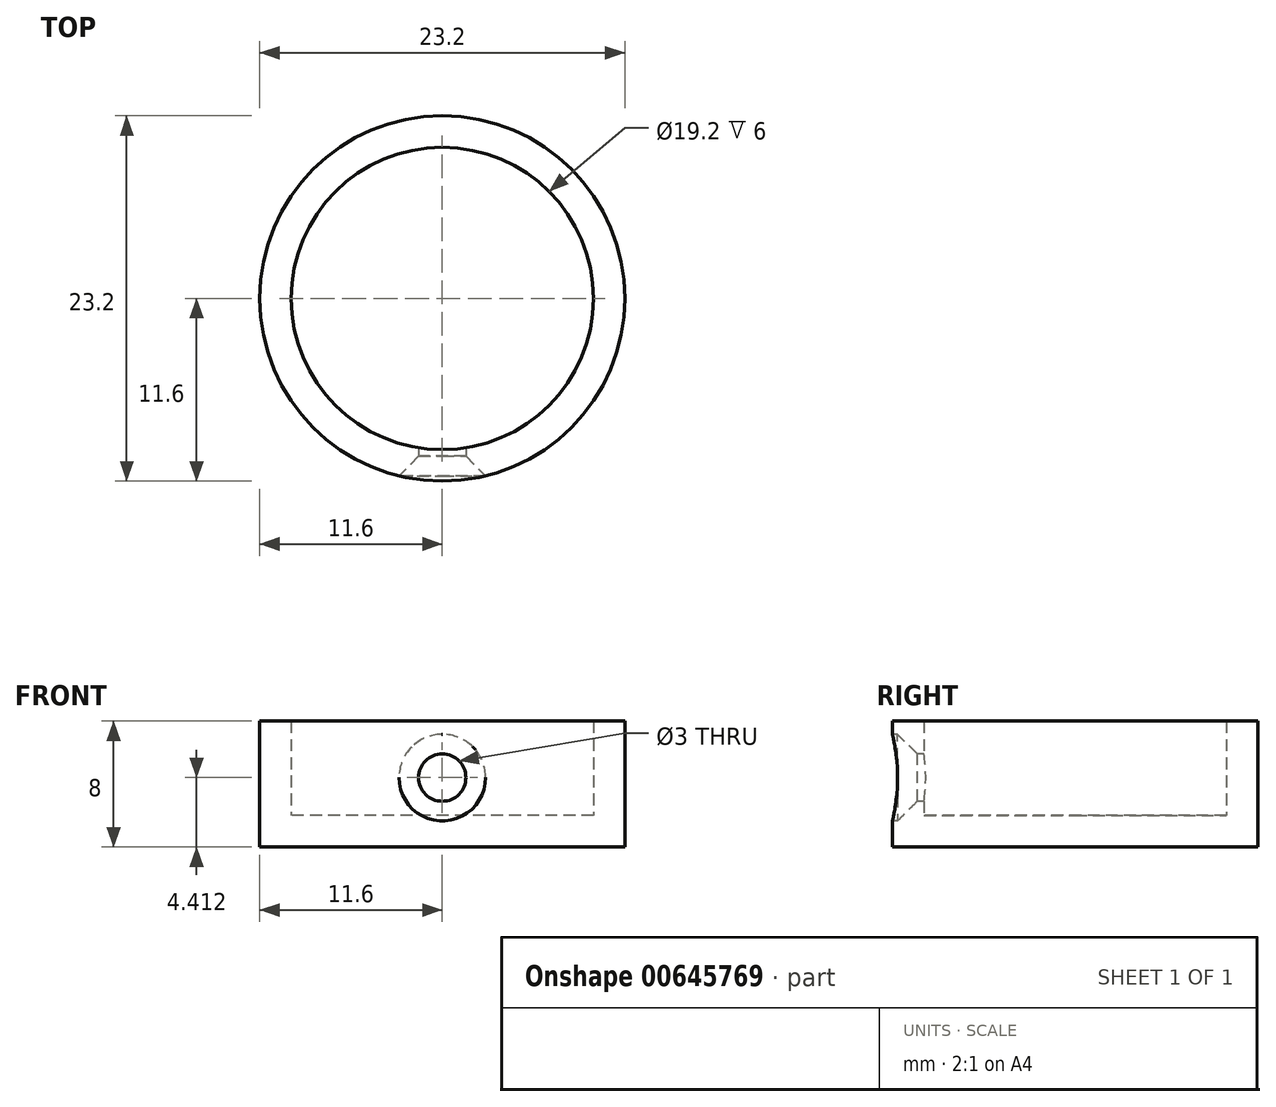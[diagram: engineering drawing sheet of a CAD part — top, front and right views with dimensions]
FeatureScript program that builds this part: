
annotation { "Feature Type Name" : "Feature", "Feature Type Description" : "" }
export const myFeature = defineFeature(function(context is Context, id is Id, definition is map)
    precondition{}
    {
        {
            var Q0;
            Q0=qCreatedBy(makeId("Top.planeOp"),FACE);
            var sketch = newSketch(context, id + "F0", { "sketchPlane" : qUnion([Q0])});
            skCircle(sketch, "E0", {"center": v(0, 0) * mm, "radius": 9.6 * mm});
            skCircle(sketch, "E1", {"center": v(0, 0) * mm, "radius": 11.6 * mm});
            skPoint(sketch, "E2", {"position": v(0, -11.6) * mm});
            skLineSegment(sketch, "E3", {"start": v(8.99, -11.6) * mm, "end": v(-12.5, -11.6) * mm, "construction": true});
            skSolve(sketch);
        }
        {
            var Q0;
            Q0=makeQuery(id+"F0.imprint","IMPRINT",FACE,{"disambiguationData":[TD([[makeQuery(id+"F0.imprint","IMPRINT",EDGE,{"derivedFrom":sQuery(id+"F0.wireOp",EDGE,"E0")}),-1.0]])]});
            var Q1;
            Q1=makeQuery(id+"F0.imprint","IMPRINT",FACE,{"disambiguationData":[TD([[makeQuery(id+"F0.imprint","IMPRINT",EDGE,{"derivedFrom":sQuery(id+"F0.wireOp",EDGE,"E0")}),1.0]])]});
            extrude(context, id + "F1", {"entities" : qUnion([Q0, Q1]), "oppositeDirection" : true, "depth" : 2 * mm, "offsetDistance" : 25 * mm});
        }
        {
            var Q0;
            Q0=makeQuery(id+"F0.imprint","IMPRINT",FACE,{"disambiguationData":[TD([[makeQuery(id+"F0.imprint","IMPRINT",EDGE,{"derivedFrom":sQuery(id+"F0.wireOp",EDGE,"E0")}),-1.0]])]});
            extrude(context, id + "F2", {"entities" : qUnion([Q0]), "operationType" : NewBodyOperationType.ADD, "depth" : 6 * mm, "offsetDistance" : 25 * mm});
        }
        {
            var Q0;
            Q0=makeQuery(id+"F2.opExtrude","CAP_FACE",FACE,{"disambiguationData":[OSD([sQuery(id+"F0.wireOp",EDGE,"E0"),sQuery(id+"F0.wireOp",EDGE,"E1")])],"isStart":false});
            var sketch = newSketch(context, id + "F3", { "sketchPlane" : qUnion([Q0])});
            skPoint(sketch, "E4", {"position": v(0, -11.6) * mm});
            skSolve(sketch);
        }
        {
            var Q0;
            Q0=sQuery(id+"F3.wireOp",VERTEX,"E4");
            var Q1;
            Q1=sQuery(id+"F0.wireOp",VERTEX,"E3.start");
            var Q2;
            Q2=sQuery(id+"F0.wireOp",VERTEX,"E3.end");
            cPlane(context, id + "F4", {"entities" : qUnion([Q0, Q1, Q2]), "cplaneType" : CPlaneType.THREE_POINT, "offset" : 25 * mm, "width" : 150 * mm, "height" : 150 * mm});
        }
        {
            var Q0;
            Q0=qCreatedBy(id+"F4.planeOp",FACE);
            var sketch = newSketch(context, id + "F5", { "sketchPlane" : qUnion([Q0])});
            skPoint(sketch, "E5", {"position": v(0, 2.41) * mm});
            skSolve(sketch);
        }
        {
            var Q0;
            Q0=sQuery(id+"F5.wireOp",VERTEX,"E5");
            var Q1;
            Q1=makeQuery(id+"F1.opExtrude","SWEPT_BODY",BODY,{"disambiguationData":[OSD([sQuery(id+"F0.wireOp",EDGE,"E1")])]});
            hole(context, id + "F6", {"style" : HoleStyle.C_SINK, "endStyle" : HoleEndStyle.BLIND, "holeDiameter" : 3 * mm, "cSinkDiameter" : 5.5 * mm, "cSinkAngle" : 90 * degree, "majorDiameter" : 5 * mm, "holeDepth" : 5 * mm, "isTappedThrough" : true, "tappedDepth" : 12 * mm, "tapClearance" : 3, "locations" : qUnion([Q0]), "scope" : qUnion([Q1])});
        }
    });
